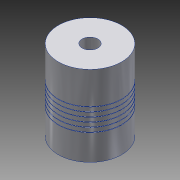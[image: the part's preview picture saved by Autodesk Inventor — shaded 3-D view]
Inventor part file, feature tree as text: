
AUTODESK INVENTOR PART (.ipt)
format: ipt  version: 2015 (Build 190159000, 159)  size: 139,264 bytes
history: native  units: in
note: dims shown in document units (in); Inventor stores cm internally (conversion verified against a paired STEP export)
features: revolve x1, sketch x1
ambient origin geometry x8: Origin, YZ Plane, XZ Plane, XY Plane, X Axis, Y Axis, Z Axis, Center Point
bodies: Body1 (feature_tree)
feature tree (2):
  revolve  "Revolution2"  [1 undecoded]
  sketch  "Sketch2"  dims[d1=0.2in d2=0.2in d3=1.0in d4=0.005in d5=0.005in d6=0.005in d7=0.005in d8=0.005in d10=0.005in d12=0.05in d13=0.05in d14=0.05in d15=0.05in d16=0.05in d17=0.0984in d18=0.1969in d20=0.3937in d21=0.2in d22=90.0deg]
note: 1 required parameter value undecoded (feature->parameter linkage not recoverable at this tier; creation-order binding heuristic only, values carry confidence <= 0.55)
